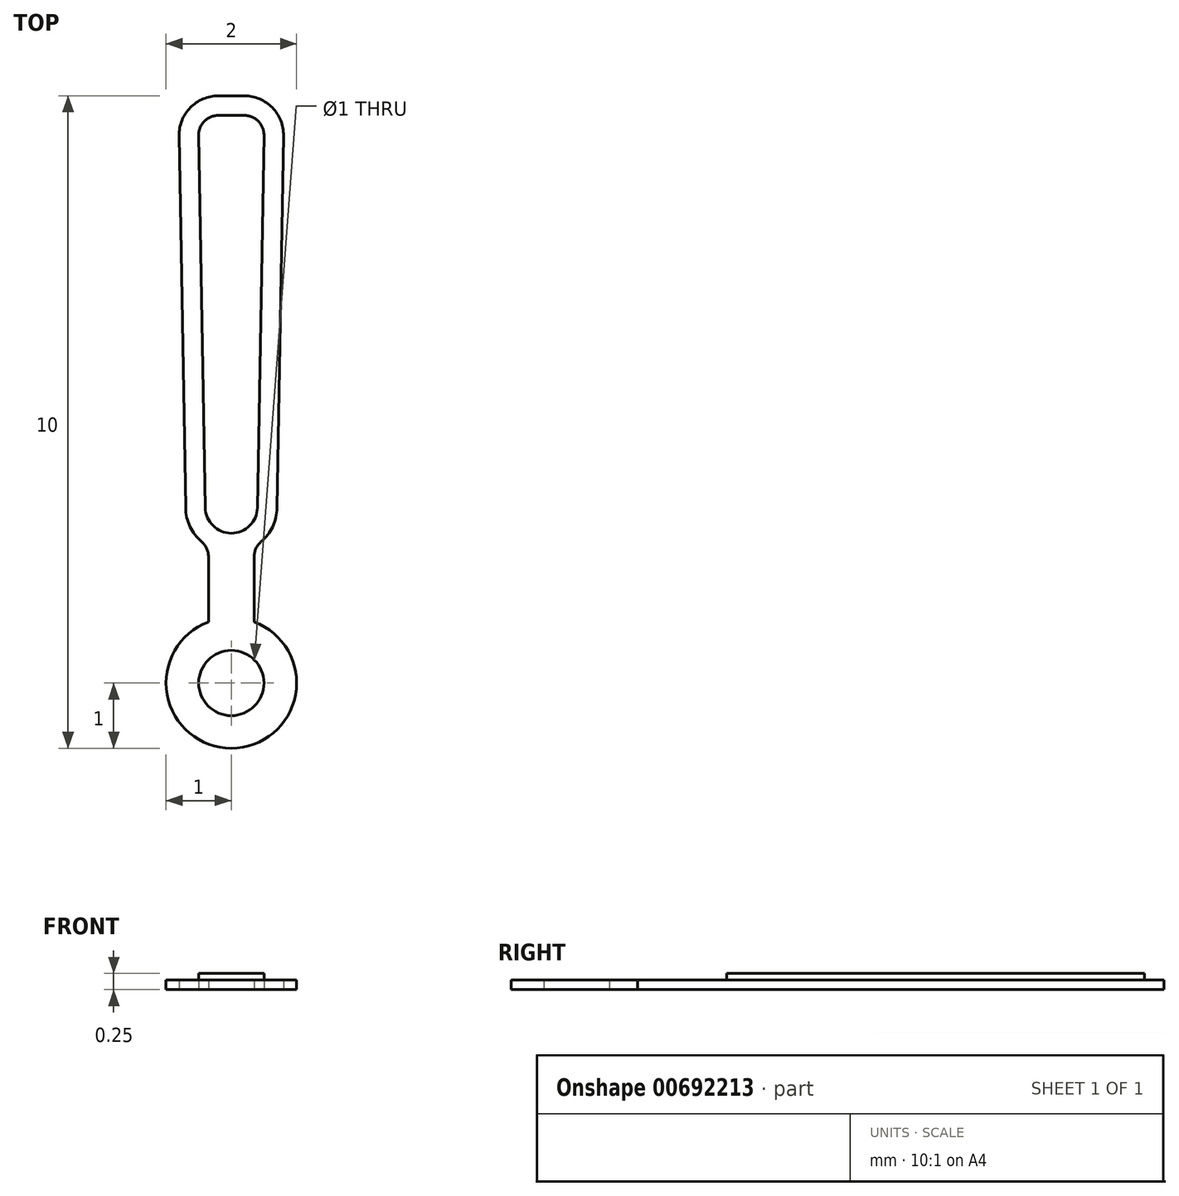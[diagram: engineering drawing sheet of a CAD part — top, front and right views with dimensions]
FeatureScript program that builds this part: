
annotation { "Feature Type Name" : "Feature", "Feature Type Description" : "" }
export const myFeature = defineFeature(function(context is Context, id is Id, definition is map)
    precondition{}
    {
        {
            var Q0;
            Q0=qCreatedBy(makeId("Top.planeOp"),FACE);
            var sketch = newSketch(context, id + "F0", { "sketchPlane" : qUnion([Q0])});
            skCircle(sketch, "E0", {"center": v(0, 0) * mm, "radius": 0.5 * mm});
            skArc(sketch, "E1", {"start": v(-0.35, 0.94) * mm, "mid": v(0, -1) * mm, "end": v(0.35, 0.94) * mm});
            skLineSegment(sketch, "E2", {"start": v(-0.35, 0.94) * mm, "end": v(-0.35, 1.94) * mm});
            skLineSegment(sketch, "E3", {"start": v(-0.7, 2.68) * mm, "end": v(-0.8, 8.39) * mm});
            skLineSegment(sketch, "E4", {"start": v(-0.2, 9) * mm, "end": v(0, 9) * mm});
            skPoint(sketch, "E5.visualSharp", {"position": v(-0.81, 9) * mm});
            skArc(sketch, "E5.filletArc", {"start": v(-0.2, 9) * mm, "mid": v(-0.63, 8.82) * mm, "end": v(-0.8, 8.39) * mm});
            skArc(sketch, "E6.filletArc", {"start": v(-0.35, 1.94) * mm, "mid": v(-0.38, 2.06) * mm, "end": v(-0.46, 2.16) * mm});
            skArc(sketch, "E7.filletArc", {"start": v(-0.7, 2.68) * mm, "mid": v(-0.63, 2.4) * mm, "end": v(-0.46, 2.16) * mm});
            skArc(sketch, "E8.0", {"start": v(-0.4, 2.69) * mm, "mid": v(-0.28, 2.41) * mm, "end": v(0, 2.3) * mm, "construction": true});
            skLineSegment(sketch, "E8.1", {"start": v(-0.4, 2.69) * mm, "end": v(-0.5, 8.4) * mm, "construction": true});
            skArc(sketch, "E8.2", {"start": v(-0.2, 8.7) * mm, "mid": v(-0.41, 8.61) * mm, "end": v(-0.5, 8.4) * mm, "construction": true});
            skLineSegment(sketch, "E8.3", {"start": v(-0.2, 8.7) * mm, "end": v(0, 8.7) * mm, "construction": true});
            skLineSegment(sketch, "E9.MirrorCS", {"start": v(0.2, 8.7) * mm, "end": v(0, 8.7) * mm, "construction": true});
            skLineSegment(sketch, "E10.MirrorCS", {"start": v(0.2, 9) * mm, "end": v(0, 9) * mm});
            skArc(sketch, "E11.MirrorCS", {"start": v(0.4, 2.69) * mm, "mid": v(0.28, 2.41) * mm, "end": v(0, 2.3) * mm, "construction": true});
            skPoint(sketch, "E12.MirrorP", {"position": v(0.81, 9) * mm});
            skLineSegment(sketch, "E13.MirrorCS", {"start": v(0.35, 0.94) * mm, "end": v(0.35, 1.94) * mm});
            skLineSegment(sketch, "E14.MirrorCS", {"start": v(0.7, 2.68) * mm, "end": v(0.8, 8.39) * mm});
            skLineSegment(sketch, "E15.MirrorCS", {"start": v(0.4, 2.69) * mm, "end": v(0.5, 8.4) * mm, "construction": true});
            skArc(sketch, "E16.MirrorCS", {"start": v(0.7, 2.68) * mm, "mid": v(0.63, 2.4) * mm, "end": v(0.46, 2.16) * mm});
            skArc(sketch, "E17.MirrorCS", {"start": v(0.2, 9) * mm, "mid": v(0.63, 8.82) * mm, "end": v(0.8, 8.39) * mm});
            skArc(sketch, "E18.MirrorCS", {"start": v(0.2, 8.7) * mm, "mid": v(0.41, 8.61) * mm, "end": v(0.5, 8.4) * mm, "construction": true});
            skArc(sketch, "E19.MirrorCS", {"start": v(0.35, 1.94) * mm, "mid": v(0.38, 2.06) * mm, "end": v(0.46, 2.16) * mm});
            skSolve(sketch);
        }
        {
            var Q0;
            Q0=makeQuery(id+"F0.imprint","IMPRINT",FACE,{"disambiguationData":[TD([[makeQuery(id+"F0.imprint","IMPRINT",EDGE,{"derivedFrom":sQuery(id+"F0.wireOp",EDGE,"E0")}),-1.0]])]});
            extrude(context, id + "F1", {"entities" : qUnion([Q0]), "depth" : 0.25 * mm, "offsetDistance" : 25 * mm});
        }
        {
            var Q0;
            Q0=makeQuery(id+"F1.opExtrude","CAP_FACE",FACE,{"disambiguationData":[OSD([sQuery(id+"F0.wireOp",EDGE,"E0"),sQuery(id+"F0.wireOp",EDGE,"E1"),sQuery(id+"F0.wireOp",EDGE,"E2"),sQuery(id+"F0.wireOp",EDGE,"E3"),sQuery(id+"F0.wireOp",EDGE,"E4"),sQuery(id+"F0.wireOp",EDGE,"E5.filletArc"),sQuery(id+"F0.wireOp",EDGE,"E6.filletArc"),sQuery(id+"F0.wireOp",EDGE,"E7.filletArc"),sQuery(id+"F0.wireOp",EDGE,"E10.MirrorCS"),sQuery(id+"F0.wireOp",EDGE,"E13.MirrorCS"),sQuery(id+"F0.wireOp",EDGE,"E14.MirrorCS"),sQuery(id+"F0.wireOp",EDGE,"E16.MirrorCS"),sQuery(id+"F0.wireOp",EDGE,"E17.MirrorCS"),sQuery(id+"F0.wireOp",EDGE,"E19.MirrorCS")])],"isStart":false});
            var sketch = newSketch(context, id + "F2", { "sketchPlane" : qUnion([Q0])});
            skArc(sketch, "E20.0", {"start": v(0.4, 2.69) * mm, "mid": v(0.28, 2.41) * mm, "end": v(0, 2.3) * mm});
            skArc(sketch, "E20.1", {"start": v(-0.4, 2.69) * mm, "mid": v(-0.28, 2.41) * mm, "end": v(0, 2.3) * mm});
            skLineSegment(sketch, "E20.2", {"start": v(-0.4, 2.69) * mm, "end": v(-0.5, 8.4) * mm});
            skLineSegment(sketch, "E20.3", {"start": v(0.4, 2.69) * mm, "end": v(0.5, 8.4) * mm});
            skArc(sketch, "E20.4", {"start": v(0.2, 8.7) * mm, "mid": v(0.41, 8.61) * mm, "end": v(0.5, 8.4) * mm});
            skLineSegment(sketch, "E20.5", {"start": v(0.2, 8.7) * mm, "end": v(0, 8.7) * mm});
            skLineSegment(sketch, "E20.6", {"start": v(-0.2, 8.7) * mm, "end": v(0, 8.7) * mm});
            skArc(sketch, "E20.7", {"start": v(-0.2, 8.7) * mm, "mid": v(-0.41, 8.61) * mm, "end": v(-0.5, 8.4) * mm});
            skPoint(sketch, "E20.8", {"position": v(-0.1, 8.7) * mm});
            skSolve(sketch);
        }
        {
            var Q0;
            Q0=makeQuery(id+"F2.imprint","IMPRINT",FACE,{"disambiguationData":[TD([[makeQuery(id+"F2.imprint","IMPRINT",EDGE,{"derivedFrom":sQuery(id+"F2.wireOp",EDGE,"E20.0")}),-1.0]])]});
            extrude(context, id + "F3", {"entities" : qUnion([Q0]), "operationType" : NewBodyOperationType.REMOVE, "oppositeDirection" : true, "depth" : 0.1 * mm, "offsetDistance" : 25 * mm});
        }
    });
